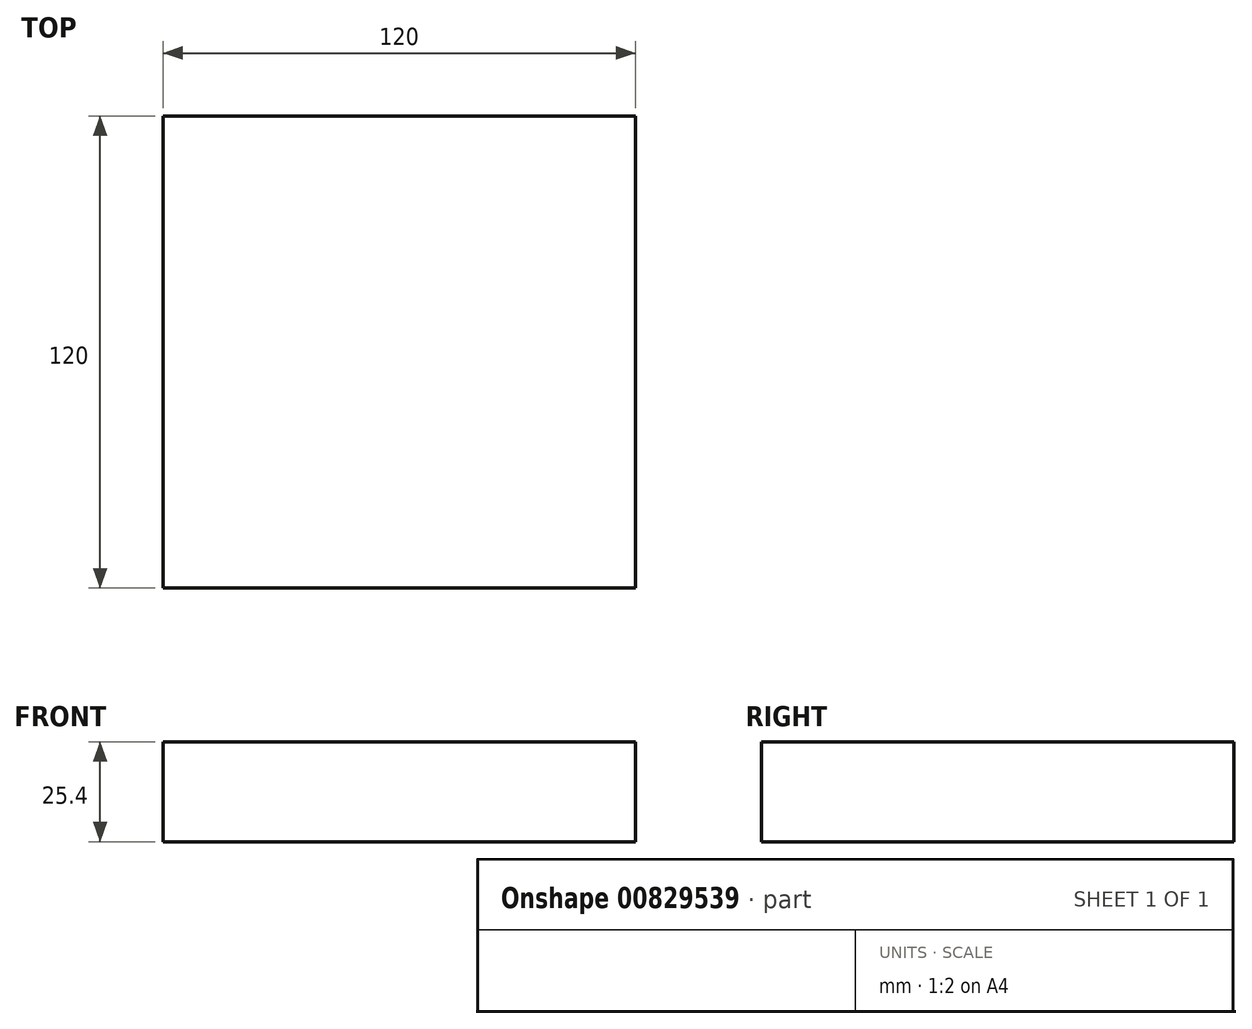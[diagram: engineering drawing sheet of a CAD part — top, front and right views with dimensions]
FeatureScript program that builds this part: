
annotation { "Feature Type Name" : "Feature", "Feature Type Description" : "" }
export const myFeature = defineFeature(function(context is Context, id is Id, definition is map)
    precondition{}
    {
        {
            var Q0;
            Q0=qCreatedBy(makeId("Top.planeOp"),FACE);
            var sketch = newSketch(context, id + "F0", { "sketchPlane" : qUnion([Q0])});
            skLineSegment(sketch, "E0.bottom", {"start": v(-60, 60) * mm, "end": v(60, 60) * mm});
            skLineSegment(sketch, "E0.top", {"start": v(-60, -60) * mm, "end": v(60, -60) * mm});
            skLineSegment(sketch, "E0.left", {"start": v(-60, 60) * mm, "end": v(-60, -60) * mm});
            skLineSegment(sketch, "E0.right", {"start": v(60, 60) * mm, "end": v(60, -60) * mm});
            skPoint(sketch, "E0.middle", {"position": v(0, 0) * mm});
            skSolve(sketch);
        }
        {
            var Q0;
            Q0=makeQuery(id+"F0.imprint","IMPRINT",FACE,{"disambiguationData":[TD([[makeQuery(id+"F0.imprint","IMPRINT",EDGE,{"derivedFrom":sQuery(id+"F0.wireOp",EDGE,"E0.bottom")}),-1.0]])]});
            extrude(context, id + "F1", {"entities" : qUnion([Q0]), "depth" : 25.4 * mm, "offsetDistance" : 25.4 * mm});
        }
    });
